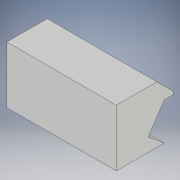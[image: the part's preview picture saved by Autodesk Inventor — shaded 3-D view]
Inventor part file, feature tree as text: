
AUTODESK INVENTOR PART (.ipt)
format: ipt  version: 2019 (Build 230136000, 136)  size: 150,016 bytes
history: native  units: in
note: dims shown in document units (in); Inventor stores cm internally (conversion verified against a paired STEP export)
features: extrude x2, plane x1, mirror x1, sketch x1
ambient origin geometry x8: Origin, YZ Plane, XZ Plane, XY Plane, X Axis, Y Axis, Z Axis, Center Point
bodies: Solid1 (feature_tree)
feature tree (5):
  extrude  "Extrusion1"  Depth=3.1496in
  extrude  "Extrusion2"  Depth=0.1969in
  plane  "Work Plane1"
  mirror  "Mirror1"
  sketch  "Sketch3"  dims[d0=3.7402in d2=3.1496in d5=0.3436in d12=7.0in d13=0.0in d20=0.1969in d22=0.1969in d23=0.1969in d24=1.0827in d27=0.1969in d28=0.1969in d29=0.1969in d30=0.3462in d31=3.7402in d32=2.6575in d34=2.7149in d35=0.1969in d36=1.0827in d37=1.378in d39=0.5906in d40=1.5749in d41=0.1969in d42=0.0in]
